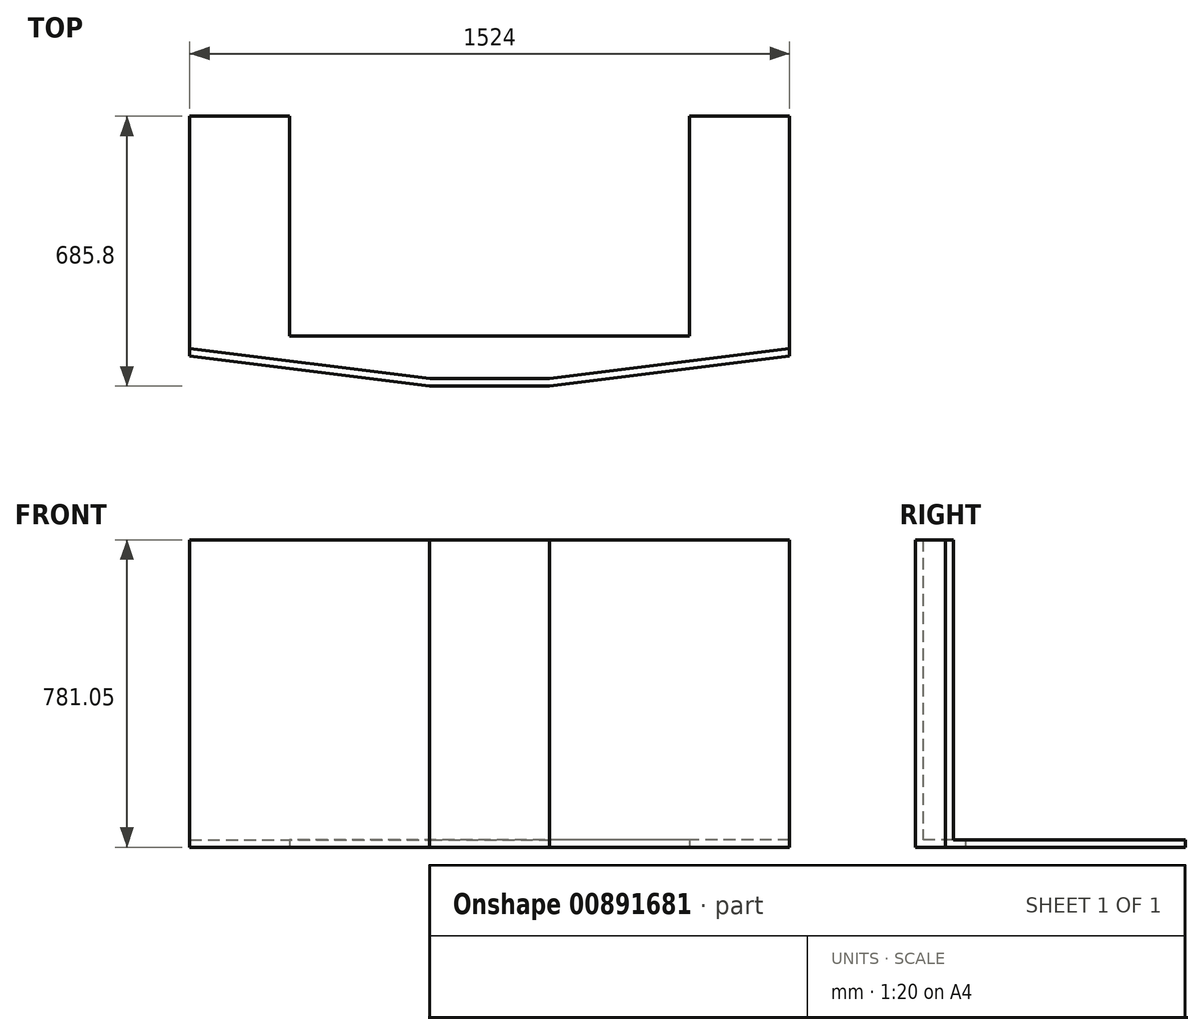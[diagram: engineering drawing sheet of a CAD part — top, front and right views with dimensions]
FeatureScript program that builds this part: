
annotation { "Feature Type Name" : "Feature", "Feature Type Description" : "" }
export const myFeature = defineFeature(function(context is Context, id is Id, definition is map)
    precondition{}
    {
        {
            var Q0;
            Q0=qCreatedBy(makeId("Top.planeOp"),FACE);
            var sketch = newSketch(context, id + "F0", { "sketchPlane" : qUnion([Q0])});
            skLineSegment(sketch, "E0", {"start": v(-152.4, -539.65) * mm, "end": v(0, -539.65) * mm});
            skLineSegment(sketch, "E1", {"start": v(-152.4, -539.65) * mm, "end": v(-762, -539.65) * mm, "construction": true});
            skLineSegment(sketch, "E2", {"start": v(-762, -539.65) * mm, "end": v(-762, -463.45) * mm, "construction": true});
            skLineSegment(sketch, "E3", {"start": v(-762, -463.45) * mm, "end": v(-152.4, -539.65) * mm});
            skLineSegment(sketch, "E4", {"start": v(-762, -463.45) * mm, "end": v(-762, 146.15) * mm});
            skLineSegment(sketch, "E5", {"start": v(-762, 146.15) * mm, "end": v(-508, 146.15) * mm});
            skLineSegment(sketch, "E6", {"start": v(-508, 146.15) * mm, "end": v(-508, -412.65) * mm});
            skLineSegment(sketch, "E7", {"start": v(-508, -412.65) * mm, "end": v(0, -412.65) * mm});
            skLineSegment(sketch, "E8", {"start": v(0, -539.65) * mm, "end": v(0, 902.5) * mm, "construction": true});
            skLineSegment(sketch, "E9.MirrorCS", {"start": v(762, 146.15) * mm, "end": v(508, 146.15) * mm});
            skLineSegment(sketch, "E10.MirrorCS", {"start": v(508, 146.15) * mm, "end": v(508, -412.65) * mm});
            skLineSegment(sketch, "E11.MirrorCS", {"start": v(762, -463.45) * mm, "end": v(762, 146.15) * mm});
            skLineSegment(sketch, "E12.MirrorCS", {"start": v(508, -412.65) * mm, "end": v(0, -412.65) * mm});
            skLineSegment(sketch, "E13.MirrorCS", {"start": v(762, -463.45) * mm, "end": v(152.4, -539.65) * mm});
            skLineSegment(sketch, "E14.MirrorCS", {"start": v(152.4, -539.65) * mm, "end": v(0, -539.65) * mm});
            skLineSegment(sketch, "E15.MirrorCS", {"start": v(152.4, -539.65) * mm, "end": v(762, -539.65) * mm, "construction": true});
            skLineSegment(sketch, "E16.MirrorCS", {"start": v(762, -539.65) * mm, "end": v(762, -463.45) * mm, "construction": true});
            skSolve(sketch);
        }
        {
            var Q0;
            Q0 = qSketchRegion(id + "F0", true);
            extrude(context, id + "F1", {"entities" : qUnion([Q0]), "depth" : 19.05 * mm, "offsetDistance" : 25.4 * mm});
        }
        {
            var Q0;
            Q0=makeQuery(id+"F1.opExtrude","CAP_FACE",FACE,{"disambiguationData":[OSD([sQuery(id+"F0.wireOp",EDGE,"E0"),sQuery(id+"F0.wireOp",EDGE,"E3"),sQuery(id+"F0.wireOp",EDGE,"E4"),sQuery(id+"F0.wireOp",EDGE,"E5"),sQuery(id+"F0.wireOp",EDGE,"E6"),sQuery(id+"F0.wireOp",EDGE,"E7"),sQuery(id+"F0.wireOp",EDGE,"E9.MirrorCS"),sQuery(id+"F0.wireOp",EDGE,"E10.MirrorCS"),sQuery(id+"F0.wireOp",EDGE,"E11.MirrorCS"),sQuery(id+"F0.wireOp",EDGE,"E12.MirrorCS"),sQuery(id+"F0.wireOp",EDGE,"E13.MirrorCS"),sQuery(id+"F0.wireOp",EDGE,"E14.MirrorCS")])],"isStart":false});
            var sketch = newSketch(context, id + "F2", { "sketchPlane" : qUnion([Q0])});
            skLineSegment(sketch, "E17.0", {"start": v(-762, -444.25) * mm, "end": v(-151.21, -520.6) * mm});
            skLineSegment(sketch, "E18.0", {"start": v(-151.21, -520.6) * mm, "end": v(151.21, -520.6) * mm});
            skLineSegment(sketch, "E19.0", {"start": v(762, -444.25) * mm, "end": v(151.21, -520.6) * mm});
            skLineSegment(sketch, "E20", {"start": v(762, -463.45) * mm, "end": v(762, -444.25) * mm});
            skLineSegment(sketch, "E21", {"start": v(762, -463.45) * mm, "end": v(152.4, -539.65) * mm});
            skLineSegment(sketch, "E22", {"start": v(152.4, -539.65) * mm, "end": v(-152.4, -539.65) * mm});
            skLineSegment(sketch, "E23", {"start": v(-152.4, -539.65) * mm, "end": v(-762, -463.45) * mm});
            skLineSegment(sketch, "E24", {"start": v(-762, -463.45) * mm, "end": v(-762, -444.25) * mm});
            skSolve(sketch);
        }
        {
            var Q0;
            Q0 = qSketchRegion(id + "F2", true);
            extrude(context, id + "F3", {"entities" : qUnion([Q0]), "operationType" : NewBodyOperationType.ADD, "depth" : 762 * mm, "offsetDistance" : 25.4 * mm});
        }
    });
